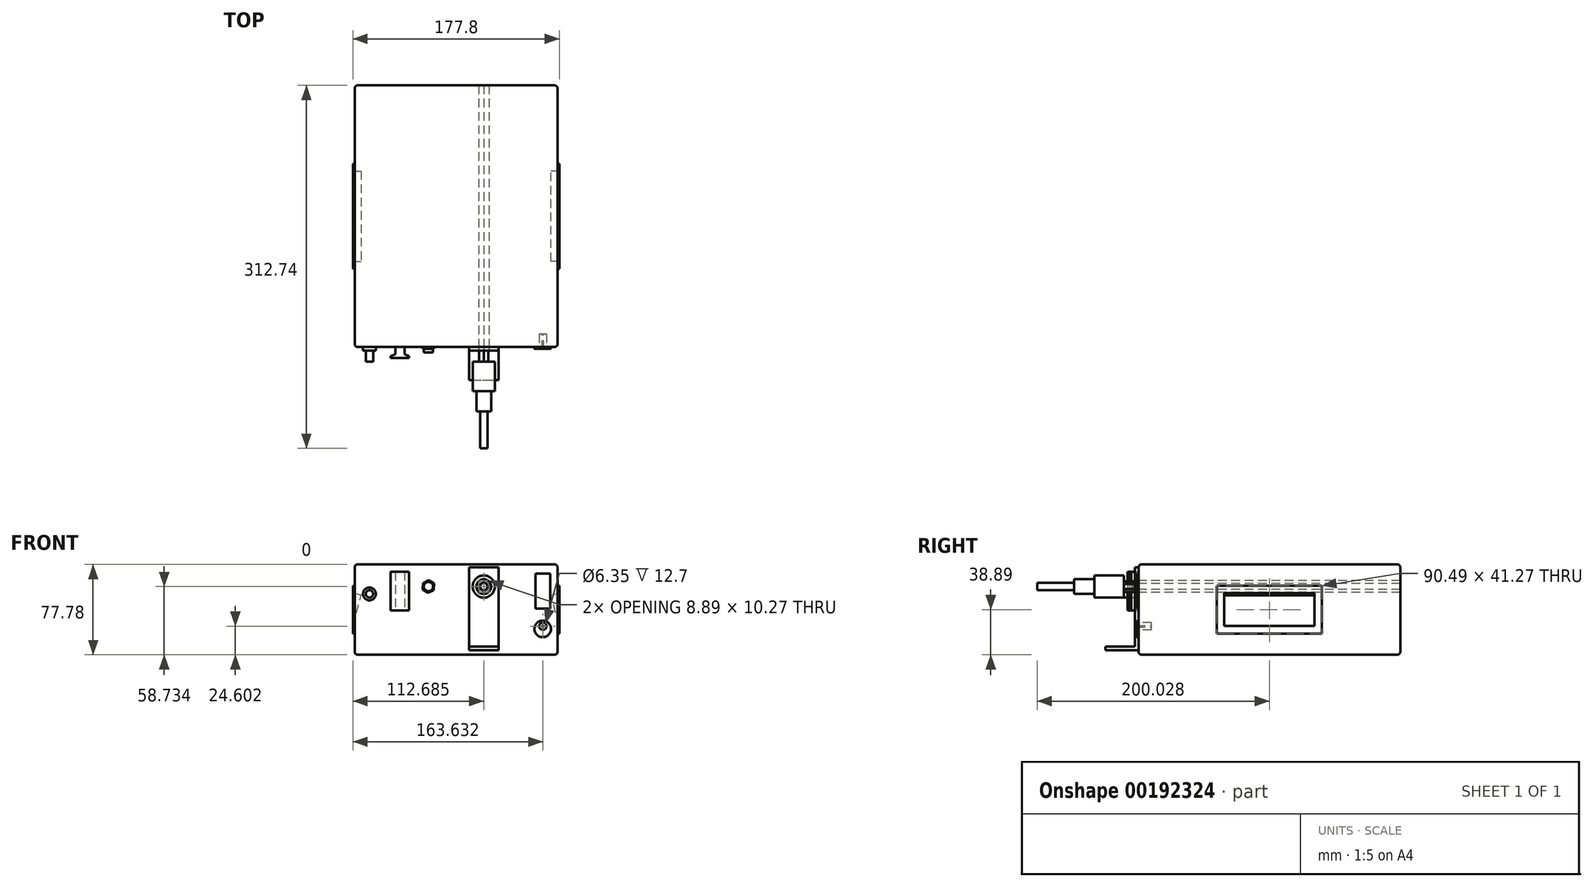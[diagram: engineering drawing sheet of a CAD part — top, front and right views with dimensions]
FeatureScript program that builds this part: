
annotation { "Feature Type Name" : "Feature", "Feature Type Description" : "" }
export const myFeature = defineFeature(function(context is Context, id is Id, definition is map)
    precondition{}
    {
        {
            var Q0;
            Q0=qCreatedBy(makeId("Front.planeOp"),FACE);
            var sketch = newSketch(context, id + "F0", { "sketchPlane" : qUnion([Q0])});
            skLineSegment(sketch, "E0.bottom", {"start": v(-87.31, 38.9) * mm, "end": v(87.31, 38.9) * mm});
            skLineSegment(sketch, "E0.top", {"start": v(-87.31, -38.9) * mm, "end": v(87.31, -38.9) * mm});
            skLineSegment(sketch, "E0.left", {"start": v(-87.31, 38.9) * mm, "end": v(-87.31, -38.9) * mm});
            skLineSegment(sketch, "E0.right", {"start": v(87.31, 38.9) * mm, "end": v(87.31, -38.9) * mm});
            skPoint(sketch, "E0.middle", {"position": v(0, 0) * mm});
            skSolve(sketch);
        }
        {
            var Q0;
            Q0 = qSketchRegion(id + "F0", true);
            extrude(context, id + "F1", {"entities" : qUnion([Q0]), "depth" : 225.42 * mm});
        }
        {
            var Q0;
            Q0=makeQuery(id+"F1.opExtrude","SWEPT_FACE",FACE,{"disambiguationData":[OSD([sQuery(id+"F0.wireOp",EDGE,"E0.left")])]});
            var sketch = newSketch(context, id + "F2", { "sketchPlane" : qUnion([Q0])});
            skLineSegment(sketch, "E1.bottom", {"start": v(67.47, 20.64) * mm, "end": v(157.96, 20.64) * mm});
            skLineSegment(sketch, "E1.top", {"start": v(67.47, -20.64) * mm, "end": v(157.96, -20.64) * mm});
            skLineSegment(sketch, "E1.left", {"start": v(67.47, 20.64) * mm, "end": v(67.47, -20.64) * mm});
            skLineSegment(sketch, "E1.right", {"start": v(157.96, 20.64) * mm, "end": v(157.96, -20.64) * mm});
            skPoint(sketch, "E1.middle", {"position": v(112.71, 0) * mm});
            skLineSegment(sketch, "E2", {"start": v(112.71, 38.9) * mm, "end": v(112.71, -38.9) * mm, "construction": true});
            skSolve(sketch);
        }
        {
            var Q0;
            Q0 = qSketchRegion(id + "F2", true);
            extrude(context, id + "F3", {"entities" : qUnion([Q0]), "operationType" : NewBodyOperationType.ADD, "depth" : 1.59 * mm});
        }
        {
            var Q0;
            Q0=makeQuery(id+"F1.opExtrude","SWEPT_FACE",FACE,{"disambiguationData":[OSD([sQuery(id+"F0.wireOp",EDGE,"E0.right")])]});
            var sketch = newSketch(context, id + "F4", { "sketchPlane" : qUnion([Q0])});
            skLineSegment(sketch, "E3.bottom", {"start": v(-157.96, 20.64) * mm, "end": v(-67.47, 20.64) * mm});
            skLineSegment(sketch, "E3.top", {"start": v(-157.96, -20.64) * mm, "end": v(-67.47, -20.64) * mm});
            skLineSegment(sketch, "E3.left", {"start": v(-157.96, 20.64) * mm, "end": v(-157.96, -20.64) * mm});
            skLineSegment(sketch, "E3.right", {"start": v(-67.47, 20.64) * mm, "end": v(-67.47, -20.64) * mm});
            skPoint(sketch, "E3.middle", {"position": v(-112.71, 0) * mm});
            skLineSegment(sketch, "E4", {"start": v(-112.71, 38.9) * mm, "end": v(-112.71, -38.9) * mm, "construction": true});
            skSolve(sketch);
        }
        {
            var Q0;
            Q0 = qSketchRegion(id + "F4", true);
            extrude(context, id + "F5", {"entities" : qUnion([Q0]), "operationType" : NewBodyOperationType.ADD, "depth" : 1.59 * mm});
        }
        {
            var Q0;
            Q0=makeQuery(id+"F1.opExtrude","CAP_EDGE",EDGE,{"disambiguationData":[OSD([sQuery(id+"F0.wireOp",EDGE,"E0.bottom")])],"isStart":true});
            var Q1;
            Q1=makeQuery(id+"F1.opExtrude","CAP_EDGE",EDGE,{"disambiguationData":[OSD([sQuery(id+"F0.wireOp",EDGE,"E0.right")])],"isStart":true});
            var Q2;
            Q2=makeQuery(id+"F1.opExtrude","SWEPT_EDGE",EDGE,{"disambiguationData":[OSD([sQuery(id+"F0.wireOp",EDGE,"E0.bottom"),sQuery(id+"F0.wireOp",EDGE,"E0.right")])]});
            var Q3;
            Q3=makeQuery(id+"F1.opExtrude","SWEPT_EDGE",EDGE,{"disambiguationData":[OSD([sQuery(id+"F0.wireOp",EDGE,"E0.top"),sQuery(id+"F0.wireOp",EDGE,"E0.right")])]});
            var Q4;
            Q4=makeQuery(id+"F1.opExtrude","SWEPT_FACE",FACE,{"disambiguationData":[OSD([sQuery(id+"F0.wireOp",EDGE,"E0.bottom")])]});
            var Q5;
            Q5=makeQuery(id+"F1.opExtrude","CAP_EDGE",EDGE,{"disambiguationData":[OSD([sQuery(id+"F0.wireOp",EDGE,"E0.right")])],"isStart":false});
            var Q6;
            Q6=makeQuery(id+"F1.opExtrude","CAP_FACE",FACE,{"disambiguationData":[OSD([sQuery(id+"F0.wireOp",EDGE,"E0.bottom"),sQuery(id+"F0.wireOp",EDGE,"E0.top"),sQuery(id+"F0.wireOp",EDGE,"E0.left"),sQuery(id+"F0.wireOp",EDGE,"E0.right")])],"isStart":false});
            var Q7;
            Q7=makeQuery(id+"F1.opExtrude","SWEPT_FACE",FACE,{"disambiguationData":[OSD([sQuery(id+"F0.wireOp",EDGE,"E0.top")])]});
            var Q8;
            Q8=makeQuery(id+"F1.opExtrude","CAP_FACE",FACE,{"disambiguationData":[OSD([sQuery(id+"F0.wireOp",EDGE,"E0.bottom"),sQuery(id+"F0.wireOp",EDGE,"E0.top"),sQuery(id+"F0.wireOp",EDGE,"E0.left"),sQuery(id+"F0.wireOp",EDGE,"E0.right")])],"isStart":true});
            fillet(context, id + "F6", {"entities" : qUnion([Q0, Q1, Q2, Q3, Q4, Q5, Q6, Q7, Q8]), "radius" : 2.54 * mm, "tangentPropagation" : true, "allowEdgeOverflow" : false});
        }
        {
            var Q0;
            Q0=makeQuery(id+"F3.opExtrude","CAP_FACE",FACE,{"disambiguationData":[OSD([sQuery(id+"F2.wireOp",EDGE,"E1.bottom"),sQuery(id+"F2.wireOp",EDGE,"E1.top"),sQuery(id+"F2.wireOp",EDGE,"E1.left"),sQuery(id+"F2.wireOp",EDGE,"E1.right")])],"isStart":false});
            var sketch = newSketch(context, id + "F7", { "sketchPlane" : qUnion([Q0])});
            skLineSegment(sketch, "E5", {"start": v(67.47, -14.29) * mm, "end": v(157.96, -14.29) * mm, "construction": true});
            skSolve(sketch);
        }
        {
            var Q0;
            Q0=makeQuery(id+"F7.imprint","IMPRINT",FACE,{"disambiguationData":[TD([[makeQuery(id+"F7.imprint","IMPRINT",EDGE,{"derivedFrom":makeQuery(id+"F3.opExtrude","CAP_EDGE",EDGE,{"disambiguationData":[OSD([sQuery(id+"F2.wireOp",EDGE,"E1.bottom")])],"isStart":false})}),-1.0]])]});
            var Q1;
            Q1=sQuery(id+"F7.wireOp",EDGE,"E5");
            cPlane(context, id + "F8", {"entities" : qUnion([Q0, Q1]), "cplaneType" : CPlaneType.LINE_ANGLE, "offset" : 25.4 * mm, "angle" : 345 * degree, "width" : 152.4 * mm, "height" : 152.4 * mm});
        }
        {
            var Q0;
            Q0=qCreatedBy(id+"F8.planeOp",FACE);
            var sketch = newSketch(context, id + "F9", { "sketchPlane" : qUnion([Q0])});
            skLineSegment(sketch, "E6.bottom", {"start": v(-73.82, -36.6) * mm, "end": v(-151.6, -36.6) * mm});
            skLineSegment(sketch, "E6.top", {"start": v(-73.82, -9.01) * mm, "end": v(-151.6, -9.01) * mm});
            skLineSegment(sketch, "E6.left", {"start": v(-73.82, -36.6) * mm, "end": v(-73.82, -9.01) * mm});
            skLineSegment(sketch, "E6.right", {"start": v(-151.6, -36.6) * mm, "end": v(-151.6, -9.01) * mm});
            skSolve(sketch);
        }
        {
            var Q0;
            Q0 = qSketchRegion(id + "F9", true);
            extrude(context, id + "F10", {"entities" : qUnion([Q0]), "operationType" : NewBodyOperationType.REMOVE, "oppositeDirection" : true, "depth" : 25.4 * mm});
        }
        {
            var Q0;
            Q0=makeQuery(id+"F5.opExtrude","CAP_FACE",FACE,{"disambiguationData":[OSD([sQuery(id+"F4.wireOp",EDGE,"E3.bottom"),sQuery(id+"F4.wireOp",EDGE,"E3.top"),sQuery(id+"F4.wireOp",EDGE,"E3.left"),sQuery(id+"F4.wireOp",EDGE,"E3.right")])],"isStart":false});
            var sketch = newSketch(context, id + "F11", { "sketchPlane" : qUnion([Q0])});
            skLineSegment(sketch, "E7", {"start": v(-157.96, -14.29) * mm, "end": v(-67.47, -14.29) * mm, "construction": true});
            skSolve(sketch);
        }
        {
            var Q0;
            Q0=makeQuery(id+"F11.imprint","IMPRINT",FACE,{"disambiguationData":[TD([[makeQuery(id+"F11.imprint","IMPRINT",EDGE,{"derivedFrom":makeQuery(id+"F5.opExtrude","CAP_EDGE",EDGE,{"disambiguationData":[OSD([sQuery(id+"F4.wireOp",EDGE,"E3.bottom")])],"isStart":false})}),-1.0]])]});
            var Q1;
            Q1=sQuery(id+"F11.wireOp",EDGE,"E7");
            cPlane(context, id + "F12", {"entities" : qUnion([Q0, Q1]), "cplaneType" : CPlaneType.LINE_ANGLE, "offset" : 25.4 * mm, "angle" : 345 * degree, "width" : 152.4 * mm, "height" : 152.4 * mm});
        }
        {
            var Q0;
            Q0=qCreatedBy(id+"F12.planeOp",FACE);
            var sketch = newSketch(context, id + "F13", { "sketchPlane" : qUnion([Q0])});
            skLineSegment(sketch, "E8.bottom", {"start": v(151.6, -36.6) * mm, "end": v(73.82, -36.6) * mm});
            skLineSegment(sketch, "E8.top", {"start": v(151.6, -9.42) * mm, "end": v(73.82, -9.42) * mm});
            skLineSegment(sketch, "E8.left", {"start": v(151.6, -36.6) * mm, "end": v(151.6, -9.42) * mm});
            skLineSegment(sketch, "E8.right", {"start": v(73.82, -36.6) * mm, "end": v(73.82, -9.42) * mm});
            skSolve(sketch);
        }
        {
            var Q0;
            Q0 = qSketchRegion(id + "F13", true);
            extrude(context, id + "F14", {"entities" : qUnion([Q0]), "operationType" : NewBodyOperationType.REMOVE, "oppositeDirection" : true, "depth" : 25.4 * mm});
        }
        {
            var Q0;
            Q0=makeQuery(id+"F1.opExtrude","CAP_FACE",FACE,{"disambiguationData":[OSD([sQuery(id+"F0.wireOp",EDGE,"E0.bottom"),sQuery(id+"F0.wireOp",EDGE,"E0.top"),sQuery(id+"F0.wireOp",EDGE,"E0.left"),sQuery(id+"F0.wireOp",EDGE,"E0.right")])],"isStart":false});
            var sketch = newSketch(context, id + "F15", { "sketchPlane" : qUnion([Q0])});
            skCircle(sketch, "E9", {"center": v(74.61, -16.67) * mm, "radius": 7.14 * mm});
            skSolve(sketch);
        }
        {
            var Q0;
            Q0 = qSketchRegion(id + "F15", true);
            extrude(context, id + "F16", {"entities" : qUnion([Q0]), "operationType" : NewBodyOperationType.ADD, "depth" : 1.59 * mm});
        }
        {
            var Q0;
            Q0=makeQuery(id+"F16.opExtrude","CAP_FACE",FACE,{"disambiguationData":[OSD([sQuery(id+"F15.wireOp",EDGE,"E9")])],"isStart":false});
            var sketch = newSketch(context, id + "F17", { "sketchPlane" : qUnion([Q0])});
            skCircle(sketch, "E10", {"center": v(74.73, -14.29) * mm, "radius": 3.18 * mm});
            skLineSegment(sketch, "E11", {"start": v(74.73, -14.29) * mm, "end": v(74.73, -9.53) * mm, "construction": true});
            skSolve(sketch);
        }
        {
            var Q0;
            Q0 = qSketchRegion(id + "F17", true);
            extrude(context, id + "F18", {"entities" : qUnion([Q0]), "operationType" : NewBodyOperationType.REMOVE, "oppositeDirection" : true, "depth" : 12.7 * mm});
        }
        {
            var Q0;
            Q0=makeQuery(id+"F18.boolean.opBoolean","COPY",FACE,{"derivedFrom":makeQuery(id+"F18.opExtrude","CAP_FACE",FACE,{"disambiguationData":[OSD([sQuery(id+"F17.wireOp",EDGE,"E10")])],"isStart":false})});
            var sketch = newSketch(context, id + "F19", { "sketchPlane" : qUnion([Q0])});
            skCircle(sketch, "E12", {"center": v(74.73, -14.29) * mm, "radius": 0.64 * mm});
            skSolve(sketch);
        }
        {
            var Q0;
            Q0 = qSketchRegion(id + "F19", true);
            extrude(context, id + "F20", {"entities" : qUnion([Q0]), "operationType" : NewBodyOperationType.ADD, "depth" : 12.7 * mm});
        }
        {
            var Q0;
            Q0=makeQuery(id+"F1.opExtrude","CAP_FACE",FACE,{"disambiguationData":[OSD([sQuery(id+"F0.wireOp",EDGE,"E0.bottom"),sQuery(id+"F0.wireOp",EDGE,"E0.top"),sQuery(id+"F0.wireOp",EDGE,"E0.left"),sQuery(id+"F0.wireOp",EDGE,"E0.right")])],"isStart":false});
            var sketch = newSketch(context, id + "F21", { "sketchPlane" : qUnion([Q0])});
            skLineSegment(sketch, "E13.bottom", {"start": v(80.96, 30.96) * mm, "end": v(68.26, 30.96) * mm});
            skLineSegment(sketch, "E13.top", {"start": v(80.96, 0.8) * mm, "end": v(68.26, 0.8) * mm});
            skLineSegment(sketch, "E13.left", {"start": v(80.96, 30.96) * mm, "end": v(80.96, 0.8) * mm});
            skLineSegment(sketch, "E13.right", {"start": v(68.26, 30.96) * mm, "end": v(68.26, 0.8) * mm});
            skSolve(sketch);
        }
        {
            var Q0;
            Q0 = qSketchRegion(id + "F21", true);
            extrude(context, id + "F22", {"entities" : qUnion([Q0]), "operationType" : NewBodyOperationType.ADD, "depth" : 1.59 * mm});
        }
        {
            var Q0;
            Q0=makeQuery(id+"F1.opExtrude","CAP_FACE",FACE,{"disambiguationData":[OSD([sQuery(id+"F0.wireOp",EDGE,"E0.bottom"),sQuery(id+"F0.wireOp",EDGE,"E0.top"),sQuery(id+"F0.wireOp",EDGE,"E0.left"),sQuery(id+"F0.wireOp",EDGE,"E0.right")])],"isStart":false});
            var sketch = newSketch(context, id + "F23", { "sketchPlane" : qUnion([Q0])});
            skCircle(sketch, "E14.cCircle", {"center": v(23.81, 19.84) * mm, "radius": 3.97 * mm, "construction": true});
            skLineSegment(sketch, "E14.0", {"start": v(27.8, 17.58) * mm, "end": v(23.84, 15.26) * mm});
            skLineSegment(sketch, "E14.1", {"start": v(23.84, 15.26) * mm, "end": v(19.86, 17.53) * mm});
            skLineSegment(sketch, "E14.2", {"start": v(19.86, 17.53) * mm, "end": v(19.83, 22.11) * mm});
            skLineSegment(sketch, "E14.3", {"start": v(19.83, 22.11) * mm, "end": v(23.79, 24.43) * mm});
            skLineSegment(sketch, "E14.4", {"start": v(23.79, 24.43) * mm, "end": v(27.77, 22.16) * mm});
            skLineSegment(sketch, "E14.5", {"start": v(27.77, 22.16) * mm, "end": v(27.8, 17.58) * mm});
            skPoint(sketch, "E14.0.midPoint", {"position": v(25.82, 16.42) * mm});
            skSolve(sketch);
        }
        {
            var Q0;
            Q0 = qSketchRegion(id + "F23", true);
            extrude(context, id + "F24", {"entities" : qUnion([Q0]), "operationType" : NewBodyOperationType.ADD, "depth" : 12.7 * mm});
        }
        {
            var Q0;
            Q0=makeQuery(id+"F24.opExtrude","CAP_FACE",FACE,{"disambiguationData":[OSD([sQuery(id+"F23.wireOp",EDGE,"E14.0"),sQuery(id+"F23.wireOp",EDGE,"E14.1"),sQuery(id+"F23.wireOp",EDGE,"E14.2"),sQuery(id+"F23.wireOp",EDGE,"E14.3"),sQuery(id+"F23.wireOp",EDGE,"E14.4"),sQuery(id+"F23.wireOp",EDGE,"E14.5")])],"isStart":false});
            var sketch = newSketch(context, id + "F25", { "sketchPlane" : qUnion([Q0])});
            skLineSegment(sketch, "E15", {"start": v(23.79, 24.43) * mm, "end": v(23.84, 15.26) * mm, "construction": true});
            skLineSegment(sketch, "E16", {"start": v(19.84, 19.82) * mm, "end": v(27.78, 19.82) * mm, "construction": true});
            skCircle(sketch, "E17", {"center": v(23.81, 19.84) * mm, "radius": 9.53 * mm});
            skSolve(sketch);
        }
        {
            var Q0;
            Q0 = qSketchRegion(id + "F25", true);
            extrude(context, id + "F26", {"entities" : qUnion([Q0]), "depth" : 25.4 * mm});
        }
        {
            var Q0;
            Q0=makeQuery(id+"F26.opExtrude","CAP_FACE",FACE,{"disambiguationData":[OSD([sQuery(id+"F25.wireOp",EDGE,"E17")])],"isStart":false});
            var sketch = newSketch(context, id + "F27", { "sketchPlane" : qUnion([Q0])});
            skCircle(sketch, "E18", {"center": v(23.81, 19.84) * mm, "radius": 6.35 * mm});
            skSolve(sketch);
        }
        {
            var Q0;
            Q0 = qSketchRegion(id + "F27", true);
            extrude(context, id + "F28", {"entities" : qUnion([Q0]), "operationType" : NewBodyOperationType.ADD, "depth" : 17.46 * mm});
        }
        {
            var Q0;
            Q0=makeQuery(id+"F28.opExtrude","CAP_FACE",FACE,{"disambiguationData":[OSD([sQuery(id+"F27.wireOp",EDGE,"E18")])],"isStart":false});
            var sketch = newSketch(context, id + "F29", { "sketchPlane" : qUnion([Q0])});
            skCircle(sketch, "E19", {"center": v(23.81, 19.84) * mm, "radius": 3.18 * mm});
            skSolve(sketch);
        }
        {
            var Q0;
            Q0 = qSketchRegion(id + "F29", true);
            extrude(context, id + "F30", {"entities" : qUnion([Q0]), "operationType" : NewBodyOperationType.ADD, "depth" : 31.75 * mm});
        }
        {
            var Q0;
            Q0=makeQuery(id+"F1.opExtrude","CAP_FACE",FACE,{"disambiguationData":[OSD([sQuery(id+"F0.wireOp",EDGE,"E0.bottom"),sQuery(id+"F0.wireOp",EDGE,"E0.top"),sQuery(id+"F0.wireOp",EDGE,"E0.left"),sQuery(id+"F0.wireOp",EDGE,"E0.right")])],"isStart":false});
            var sketch = newSketch(context, id + "F31", { "sketchPlane" : qUnion([Q0])});
            skCircle(sketch, "E20.cCircle", {"center": v(-23.81, 19.84) * mm, "radius": 4.76 * mm, "construction": true});
            skLineSegment(sketch, "E20.0", {"start": v(-19.18, 16.87) * mm, "end": v(-24.07, 14.35) * mm});
            skLineSegment(sketch, "E20.1", {"start": v(-24.07, 14.35) * mm, "end": v(-28.7, 17.32) * mm});
            skLineSegment(sketch, "E20.2", {"start": v(-28.7, 17.32) * mm, "end": v(-28.44, 22.81) * mm});
            skLineSegment(sketch, "E20.3", {"start": v(-28.44, 22.81) * mm, "end": v(-23.55, 25.34) * mm});
            skLineSegment(sketch, "E20.4", {"start": v(-23.55, 25.34) * mm, "end": v(-18.93, 22.37) * mm});
            skLineSegment(sketch, "E20.5", {"start": v(-18.93, 22.37) * mm, "end": v(-19.18, 16.87) * mm});
            skPoint(sketch, "E20.0.midPoint", {"position": v(-21.63, 15.61) * mm});
            skSolve(sketch);
        }
        {
            var Q0;
            Q0 = qSketchRegion(id + "F31", true);
            extrude(context, id + "F32", {"entities" : qUnion([Q0]), "operationType" : NewBodyOperationType.ADD, "depth" : 1.59 * mm});
        }
        {
            var Q0;
            Q0=makeQuery(id+"F32.opExtrude","CAP_FACE",FACE,{"disambiguationData":[OSD([sQuery(id+"F31.wireOp",EDGE,"E20.0"),sQuery(id+"F31.wireOp",EDGE,"E20.1"),sQuery(id+"F31.wireOp",EDGE,"E20.2"),sQuery(id+"F31.wireOp",EDGE,"E20.3"),sQuery(id+"F31.wireOp",EDGE,"E20.4"),sQuery(id+"F31.wireOp",EDGE,"E20.5")])],"isStart":false});
            var sketch = newSketch(context, id + "F33", { "sketchPlane" : qUnion([Q0])});
            skLineSegment(sketch, "E21", {"start": v(-23.55, 25.34) * mm, "end": v(-24.07, 14.35) * mm, "construction": true});
            skCircle(sketch, "E22", {"center": v(-23.81, 19.84) * mm, "radius": 3.97 * mm});
            skSolve(sketch);
        }
        {
            var Q0;
            Q0 = qSketchRegion(id + "F33", true);
            extrude(context, id + "F34", {"entities" : qUnion([Q0]), "operationType" : NewBodyOperationType.ADD, "depth" : 3.17 * mm});
        }
        {
            var Q0;
            Q0=makeQuery(id+"F1.opExtrude","CAP_FACE",FACE,{"disambiguationData":[OSD([sQuery(id+"F0.wireOp",EDGE,"E0.bottom"),sQuery(id+"F0.wireOp",EDGE,"E0.top"),sQuery(id+"F0.wireOp",EDGE,"E0.left"),sQuery(id+"F0.wireOp",EDGE,"E0.right")])],"isStart":false});
            var sketch = newSketch(context, id + "F35", { "sketchPlane" : qUnion([Q0])});
            skLineSegment(sketch, "E23.bottom", {"start": v(-52.39, 32.54) * mm, "end": v(-44.45, 32.54) * mm});
            skLineSegment(sketch, "E23.top", {"start": v(-52.39, -0.8) * mm, "end": v(-44.45, -0.8) * mm});
            skLineSegment(sketch, "E23.left", {"start": v(-52.39, 32.54) * mm, "end": v(-52.39, -0.8) * mm});
            skLineSegment(sketch, "E23.right", {"start": v(-44.45, 32.54) * mm, "end": v(-44.45, -0.8) * mm});
            skSolve(sketch);
        }
        {
            var Q0;
            Q0 = qSketchRegion(id + "F35", true);
            extrude(context, id + "F36", {"entities" : qUnion([Q0]), "operationType" : NewBodyOperationType.ADD, "depth" : 6.35 * mm});
        }
        {
            var Q0;
            Q0=makeQuery(id+"F36.opExtrude","CAP_FACE",FACE,{"disambiguationData":[OSD([sQuery(id+"F35.wireOp",EDGE,"E23.bottom"),sQuery(id+"F35.wireOp",EDGE,"E23.top"),sQuery(id+"F35.wireOp",EDGE,"E23.left"),sQuery(id+"F35.wireOp",EDGE,"E23.right")])],"isStart":false});
            cPlane(context, id + "F37", {"entities" : qUnion([Q0]), "cplaneType" : CPlaneType.OFFSET, "offset" : 1.59 * mm, "width" : 152.4 * mm, "height" : 152.4 * mm});
        }
        {
            var Q0;
            Q0=qCreatedBy(id+"F37.planeOp",FACE);
            var sketch = newSketch(context, id + "F38", { "sketchPlane" : qUnion([Q0])});
            skLineSegment(sketch, "E24.bottom", {"start": v(-56.36, 32.54) * mm, "end": v(-40.48, 32.54) * mm});
            skLineSegment(sketch, "E24.top", {"start": v(-56.36, -0.8) * mm, "end": v(-40.48, -0.8) * mm});
            skLineSegment(sketch, "E24.left", {"start": v(-56.36, 32.54) * mm, "end": v(-56.36, -0.8) * mm});
            skLineSegment(sketch, "E24.right", {"start": v(-40.48, 32.54) * mm, "end": v(-40.48, -0.8) * mm});
            skSolve(sketch);
        }
        {
            var Q1;
            Q1=makeQuery(id+"F36.opExtrude","CAP_FACE",FACE,{"disambiguationData":[OSD([sQuery(id+"F35.wireOp",EDGE,"E23.bottom"),sQuery(id+"F35.wireOp",EDGE,"E23.top"),sQuery(id+"F35.wireOp",EDGE,"E23.left"),sQuery(id+"F35.wireOp",EDGE,"E23.right")])],"isStart":false});
            var Q2;
            Q2=makeQuery(id+"F38.imprint","IMPRINT",FACE,{"disambiguationData":[TD([[makeQuery(id+"F38.imprint","IMPRINT",EDGE,{"derivedFrom":sQuery(id+"F38.wireOp",EDGE,"E24.bottom")}),-1.0]])]});
            loft(context, id + "F39", {"operationType" : NewBodyOperationType.ADD, "sheetProfilesArray" : [{ "sheetProfileEntities" : qUnion([Q1]) }, { "sheetProfileEntities" : qUnion([Q2]) }]});
        }
        {
            var Q0;
            Q0=makeQuery(id+"F39.opLoft","CAP_FACE",FACE,{"disambiguationData":[OSD([makeQuery(id+"F38.imprint","IMPRINT",FACE,{"disambiguationData":[TD([[makeQuery(id+"F38.imprint","IMPRINT",EDGE,{"derivedFrom":sQuery(id+"F38.wireOp",EDGE,"E24.bottom")}),-1.0]])]})])],"isStart":true});
            var sketch = newSketch(context, id + "F40", { "sketchPlane" : qUnion([Q0])});
            skLineSegment(sketch, "E25.bottom", {"start": v(-56.36, 32.54) * mm, "end": v(-40.48, 32.54) * mm});
            skLineSegment(sketch, "E25.top", {"start": v(-56.36, -0.8) * mm, "end": v(-40.48, -0.8) * mm});
            skLineSegment(sketch, "E25.left", {"start": v(-56.36, 32.54) * mm, "end": v(-56.36, -0.8) * mm});
            skLineSegment(sketch, "E25.right", {"start": v(-40.48, 32.54) * mm, "end": v(-40.48, -0.8) * mm});
            skSolve(sketch);
        }
        {
            var Q0;
            Q0 = qSketchRegion(id + "F40", true);
            extrude(context, id + "F41", {"entities" : qUnion([Q0]), "operationType" : NewBodyOperationType.ADD, "depth" : 1.59 * mm});
        }
        {
            var Q0;
            Q0=makeQuery(id+"F1.opExtrude","CAP_FACE",FACE,{"disambiguationData":[OSD([sQuery(id+"F0.wireOp",EDGE,"E0.bottom"),sQuery(id+"F0.wireOp",EDGE,"E0.top"),sQuery(id+"F0.wireOp",EDGE,"E0.left"),sQuery(id+"F0.wireOp",EDGE,"E0.right")])],"isStart":false});
            var sketch = newSketch(context, id + "F42", { "sketchPlane" : qUnion([Q0])});
            skCircle(sketch, "E26", {"center": v(-74.61, 13.5) * mm, "radius": 5.56 * mm});
            skSolve(sketch);
        }
        {
            var Q0;
            Q0 = qSketchRegion(id + "F42", true);
            extrude(context, id + "F43", {"entities" : qUnion([Q0]), "operationType" : NewBodyOperationType.ADD, "depth" : 3.17 * mm});
        }
        {
            var Q0;
            Q0=makeQuery(id+"F43.opExtrude","CAP_FACE",FACE,{"disambiguationData":[OSD([sQuery(id+"F42.wireOp",EDGE,"E26")])],"isStart":false});
            var sketch = newSketch(context, id + "F44", { "sketchPlane" : qUnion([Q0])});
            skCircle(sketch, "E27", {"center": v(-74.61, 13.5) * mm, "radius": 3.18 * mm});
            skSolve(sketch);
        }
        {
            var Q0;
            Q0 = qSketchRegion(id + "F44", true);
            extrude(context, id + "F45", {"entities" : qUnion([Q0]), "operationType" : NewBodyOperationType.ADD, "depth" : 9.52 * mm});
        }
        {
            var Q0;
            Q0=makeQuery(id+"F1.opExtrude","CAP_FACE",FACE,{"disambiguationData":[OSD([sQuery(id+"F0.wireOp",EDGE,"E0.bottom"),sQuery(id+"F0.wireOp",EDGE,"E0.top"),sQuery(id+"F0.wireOp",EDGE,"E0.left"),sQuery(id+"F0.wireOp",EDGE,"E0.right")])],"isStart":false});
            var sketch = newSketch(context, id + "F46", { "sketchPlane" : qUnion([Q0])});
            skLineSegment(sketch, "E28.bottom", {"start": v(11.09, -35.08) * mm, "end": v(36.49, -35.08) * mm});
            skLineSegment(sketch, "E28.top", {"start": v(11.09, 36.35) * mm, "end": v(36.49, 36.35) * mm});
            skLineSegment(sketch, "E28.left", {"start": v(11.09, -35.08) * mm, "end": v(11.09, 36.35) * mm});
            skLineSegment(sketch, "E28.right", {"start": v(36.49, -35.08) * mm, "end": v(36.49, 36.35) * mm});
            skLineSegment(sketch, "E29", {"start": v(23.79, 36.35) * mm, "end": v(23.79, -36.35) * mm, "construction": true});
            skSolve(sketch);
        }
        {
            var Q0;
            Q0 = qSketchRegion(id + "F46", true);
            extrude(context, id + "F47", {"entities" : qUnion([Q0]), "depth" : 3.17 * mm});
        }
        {
            var Q0;
            Q0=makeQuery(id+"F47.opExtrude","CAP_FACE",FACE,{"disambiguationData":[OSD([sQuery(id+"F46.wireOp",EDGE,"E28.bottom"),sQuery(id+"F46.wireOp",EDGE,"E28.top"),sQuery(id+"F46.wireOp",EDGE,"E28.left"),sQuery(id+"F46.wireOp",EDGE,"E28.right")])],"isStart":false});
            var sketch = newSketch(context, id + "F48", { "sketchPlane" : qUnion([Q0])});
            skLineSegment(sketch, "E30", {"start": v(23.79, 36.35) * mm, "end": v(23.79, -35.08) * mm, "construction": true});
            skLineSegment(sketch, "E31", {"start": v(27.76, 19.84) * mm, "end": v(19.88, 19.84) * mm, "construction": true});
            skCircle(sketch, "E32.cCircle", {"center": v(23.79, 19.84) * mm, "radius": 4.45 * mm, "construction": true});
            skLineSegment(sketch, "E32.0", {"start": v(28.23, 17.28) * mm, "end": v(23.79, 14.71) * mm});
            skLineSegment(sketch, "E32.1", {"start": v(23.79, 14.71) * mm, "end": v(19.34, 17.28) * mm});
            skLineSegment(sketch, "E32.2", {"start": v(19.34, 17.28) * mm, "end": v(19.34, 22.41) * mm});
            skLineSegment(sketch, "E32.3", {"start": v(19.34, 22.41) * mm, "end": v(23.79, 24.98) * mm});
            skLineSegment(sketch, "E32.4", {"start": v(23.79, 24.98) * mm, "end": v(28.23, 22.41) * mm});
            skLineSegment(sketch, "E32.5", {"start": v(28.23, 22.41) * mm, "end": v(28.23, 17.28) * mm});
            skPoint(sketch, "E32.0.midPoint", {"position": v(26, 16) * mm});
            skSolve(sketch);
        }
        {
            var Q0;
            Q0 = qSketchRegion(id + "F48", true);
            extrude(context, id + "F49", {"entities" : qUnion([Q0]), "operationType" : NewBodyOperationType.REMOVE, "endBound" : BoundingType.THROUGH_ALL, "oppositeDirection" : true, "depth" : 25.4 * mm});
        }
        {
            var Q0;
            Q0=makeQuery(id+"F47.opExtrude","CAP_FACE",FACE,{"disambiguationData":[OSD([sQuery(id+"F46.wireOp",EDGE,"E28.bottom"),sQuery(id+"F46.wireOp",EDGE,"E28.top"),sQuery(id+"F46.wireOp",EDGE,"E28.left"),sQuery(id+"F46.wireOp",EDGE,"E28.right")])],"isStart":false});
            var sketch = newSketch(context, id + "F50", { "sketchPlane" : qUnion([Q0])});
            skLineSegment(sketch, "E33.bottom", {"start": v(11.09, -35.08) * mm, "end": v(36.49, -35.08) * mm});
            skLineSegment(sketch, "E33.top", {"start": v(11.09, -31.9) * mm, "end": v(36.49, -31.9) * mm});
            skLineSegment(sketch, "E33.left", {"start": v(11.09, -35.08) * mm, "end": v(11.09, -31.9) * mm});
            skLineSegment(sketch, "E33.right", {"start": v(36.49, -35.08) * mm, "end": v(36.49, -31.9) * mm});
            skSolve(sketch);
        }
        {
            var Q0;
            Q0 = qSketchRegion(id + "F50", true);
            extrude(context, id + "F51", {"entities" : qUnion([Q0]), "operationType" : NewBodyOperationType.ADD, "depth" : 25.4 * mm});
        }
    });
